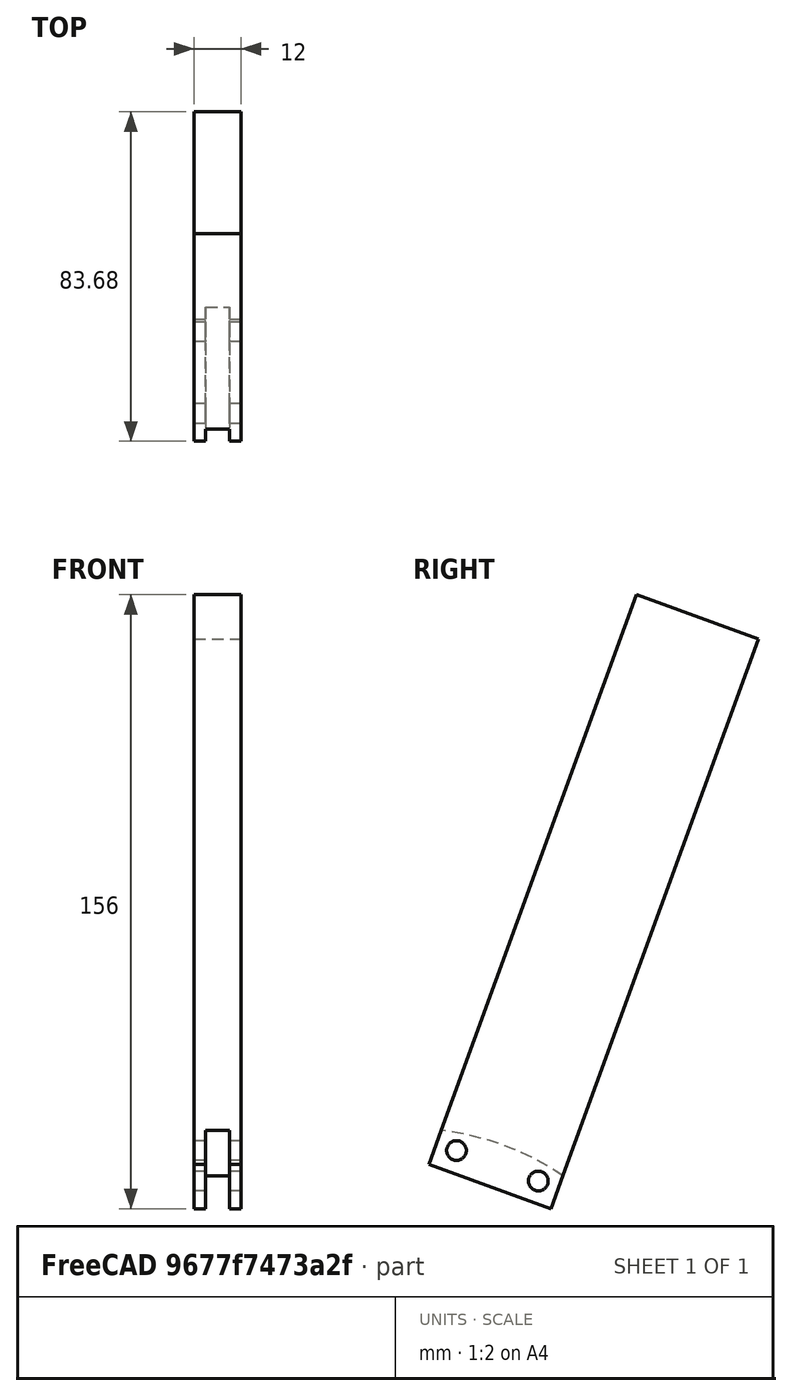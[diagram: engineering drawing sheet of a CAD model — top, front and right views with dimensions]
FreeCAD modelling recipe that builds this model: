
FCSTD DOCUMENT  (FreeCAD 0.18R16110 (Git))
Label: arm
License: All rights reserved
LicenseURL: http://en.wikipedia.org/wiki/All_rights_reserved
objects: Part::Cylinder×3, Part::Cut×3, Sketcher::SketchObject×1, Part::Extrusion×1, Mesh::Feature×1
note: 8 computed .brp shape members not serialized (recipe doc carries the construction recipe); baked Part::Feature solids carry a one-line shape summary decoded from their .brp

FEATURE [Sketcher::SketchObject] Sketch
  sketch-geometry (6):
    g0: LineSegment StartX=-6 StartY=0 StartZ=0 EndX=6 EndY=-2e-16 EndZ=0
    g1: LineSegment StartX=6 StartY=-2e-16 StartZ=0 EndX=6 EndY=9 EndZ=0
    g2: LineSegment StartX=-6 StartY=154 StartZ=0 EndX=-6 EndY=9 EndZ=0
    g3: LineSegment StartX=-6 StartY=9 StartZ=0 EndX=-6 EndY=0 EndZ=0
    g4: LineSegment StartX=-6 StartY=154 StartZ=0 EndX=6 EndY=154 EndZ=0
    g5: LineSegment StartX=6 StartY=154 StartZ=0 EndX=6 EndY=9 EndZ=0
  constraints (16):
    c: PointOnObject(g0,g-1)
    c: Coincident(g0,g1)
    c: Vertical(g1)
    c: Coincident(g2,g3)
    c: Coincident(g3,g0)
    c: Symmetric(g0,g0,g-2)
    c: Symmetric(g2,g1,g-2)
    c: DistanceX(g0,g0) = 12
    c: DistanceY(g3,g3) = 9
    c: DistanceX(g2) = -6
    c: Distance(g2) = 145
    c: Coincident(g2,g4)
    c: Coincident(g4,g5)
    c: Coincident(g5,g1)
    c: Vertical(g5)
    c: Horizontal(g4)
FEATURE [Part::Extrusion] Extrude
  Base = -> Sketch
  Dir = (0,0,1)
  DirMode = 2
  FaceMakerClass = Part::FaceMakerBullseye
  LengthFwd = 33
  LengthRev = 0
  Solid = true
  Symmetric = false
FEATURE [Part::Cylinder] Cylinder
  Angle = 360
  AttacherType = Attacher::AttachEngine3D
  Height = 6.1
  Placement = pos=(-3,-59,17) rot=(0,1,0;1.5708rad)
  Radius = 70
FEATURE [Part::Cut] Cut
  Base = -> Extrude
  Placement = pos=(0,36.22,49.58) rot=(1,0,0;1.22173rad)
  Tool = -> Cylinder
FEATURE [Part::Cylinder] Cylinder001
  Angle = 360
  AttacherType = Attacher::AttachEngine3D
  Height = 15
  Placement = pos=(7.5,33,56.6) rot=(0,-1,0;1.5708rad)
  Radius = 2.5
FEATURE [Part::Cylinder] Cylinder002
  Angle = 360
  AttacherType = Attacher::AttachEngine3D
  Height = 15
  Placement = pos=(7.5,12.2,64.35) rot=(0,-1,0;1.5708rad)
  Radius = 2.5
FEATURE [Part::Cut] Cut001
  Base = -> Cut
  Tool = -> Cylinder001
FEATURE [Part::Cut] Cut002
  Base = -> Cut001
  Tool = -> Cylinder002
FEATURE [Mesh::Feature] armscrew
  Placement = pos=(0,0,-3.2) rot=(0,0,1;0rad)
